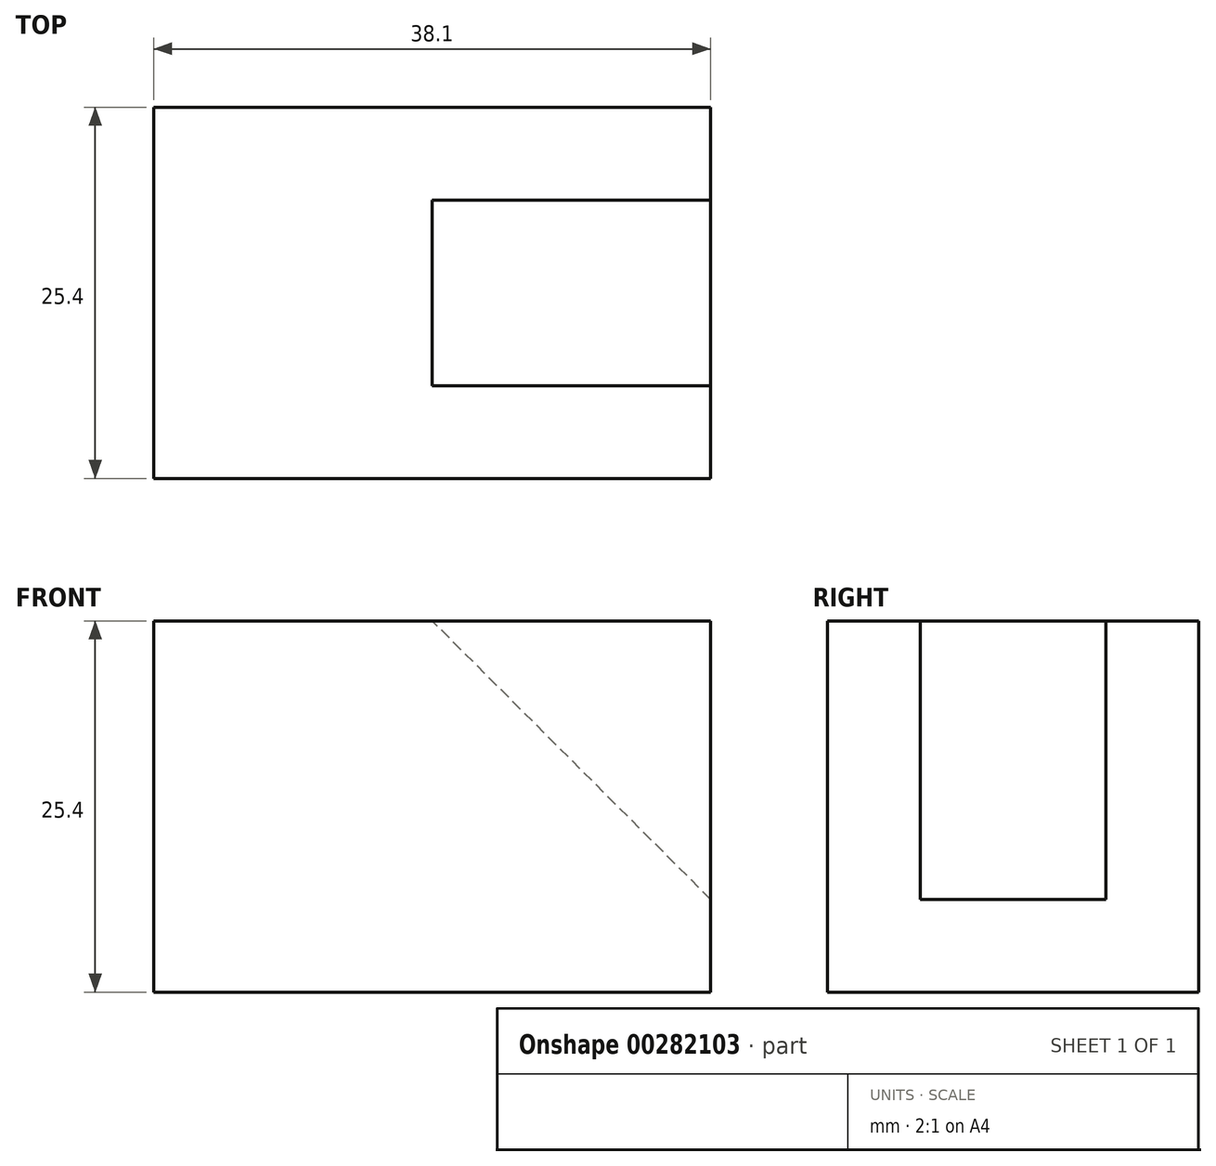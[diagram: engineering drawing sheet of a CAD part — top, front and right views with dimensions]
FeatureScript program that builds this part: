
annotation { "Feature Type Name" : "Feature", "Feature Type Description" : "" }
export const myFeature = defineFeature(function(context is Context, id is Id, definition is map)
    precondition{}
    {
        {
            var Q0;
            Q0=qCreatedBy(makeId("Front.planeOp"),FACE);
            var sketch = newSketch(context, id + "F0", { "sketchPlane" : qUnion([Q0])});
            skLineSegment(sketch, "E0", {"start": v(0, 0) * mm, "end": v(0, 25.4) * mm});
            skLineSegment(sketch, "E1", {"start": v(0, 25.4) * mm, "end": v(38.1, 25.4) * mm});
            skLineSegment(sketch, "E2", {"start": v(38.1, 25.4) * mm, "end": v(38.1, 0) * mm});
            skLineSegment(sketch, "E3", {"start": v(38.1, 0) * mm, "end": v(0, 0) * mm});
            skSolve(sketch);
        }
        {
            var Q0;
            Q0 = qSketchRegion(id + "F0", true);
            extrude(context, id + "F1", {"entities" : qUnion([Q0]), "endBound" : BoundingType.SYMMETRIC, "depth" : 25.4 * mm});
        }
        {
            var Q0;
            Q0=qCreatedBy(makeId("Front.planeOp"),FACE);
            var sketch = newSketch(context, id + "F2", { "sketchPlane" : qUnion([Q0])});
            skLineSegment(sketch, "E4", {"start": v(19.05, 25.4) * mm, "end": v(38.1, 25.4) * mm});
            skLineSegment(sketch, "E5", {"start": v(38.1, 25.4) * mm, "end": v(38.1, 6.35) * mm});
            skLineSegment(sketch, "E6", {"start": v(38.1, 6.35) * mm, "end": v(19.05, 25.4) * mm});
            skSolve(sketch);
        }
        {
            var Q0;
            Q0 = qSketchRegion(id + "F2", true);
            extrude(context, id + "F3", {"entities" : qUnion([Q0]), "operationType" : NewBodyOperationType.REMOVE, "endBound" : BoundingType.SYMMETRIC, "depth" : 12.7 * mm});
        }
    });
